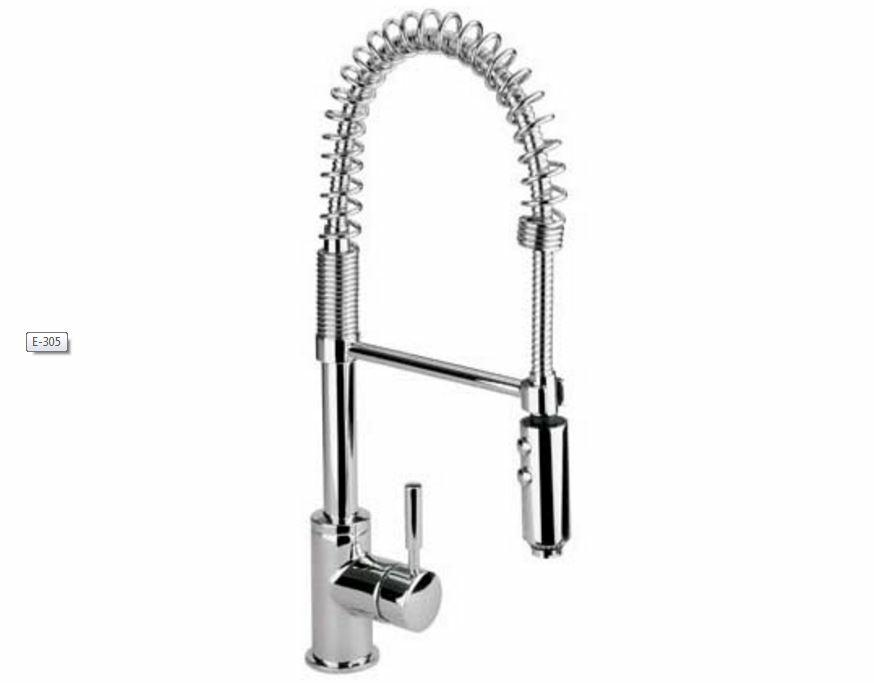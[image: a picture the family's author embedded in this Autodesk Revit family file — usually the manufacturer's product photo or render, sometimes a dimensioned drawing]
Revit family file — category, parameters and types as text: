
# Revit family: Monomando de Cocina E-305
name_source: partatom
category: Mobiliario
revit_build: Autodesk Revit 2016 (Build: 20150220_1215(x64)
units: mm (PartAtom-declared; Revit-internal decimal feet)

## family parameters
Compartido = Sí
Corte con vacíos al cargar = No
Número OmniClass = 23.45.55.14
Punto de cálculo de habitación = Sí
Se basa en plano de trabajo = No
Siempre vertical = Sí
Título OmniClass = Single Faucets

## types (1)
- E-305
    Brass Chromed = Brass
    Comentarios de tipo = Single Control Kitchen Faucet
    Data Sheet = http://www.helvex.com.mx
    Descripción = Single Control With Flexible Faucet
    Elevación por Defecto = 1"
    Fabricante = HELVEX
    Features = Single Control Ceramic Cartridge; Giratory Faucet; Device To Change a Fixed Jet Shower; Flexible Hose And Head; Includes Wrench to Install
    Imagen de tipo = E-305.JPG
    Inlet Threads = ½" - 14 NPSM
    Instructive = http://www.helvex.com.mx
    Max. Working Pressure = 85.3 psi
    Min. Working Pressure = 14.2 psi
    Modelo = E-305
    Total Height = 23"
    Total Length = 8"
    Total Width = 2"
    URL = http://www.helvex.com.mx

## geometry (parser evidence)
native form markers: Sweep x3
no freeform markers — native parametric forms only
